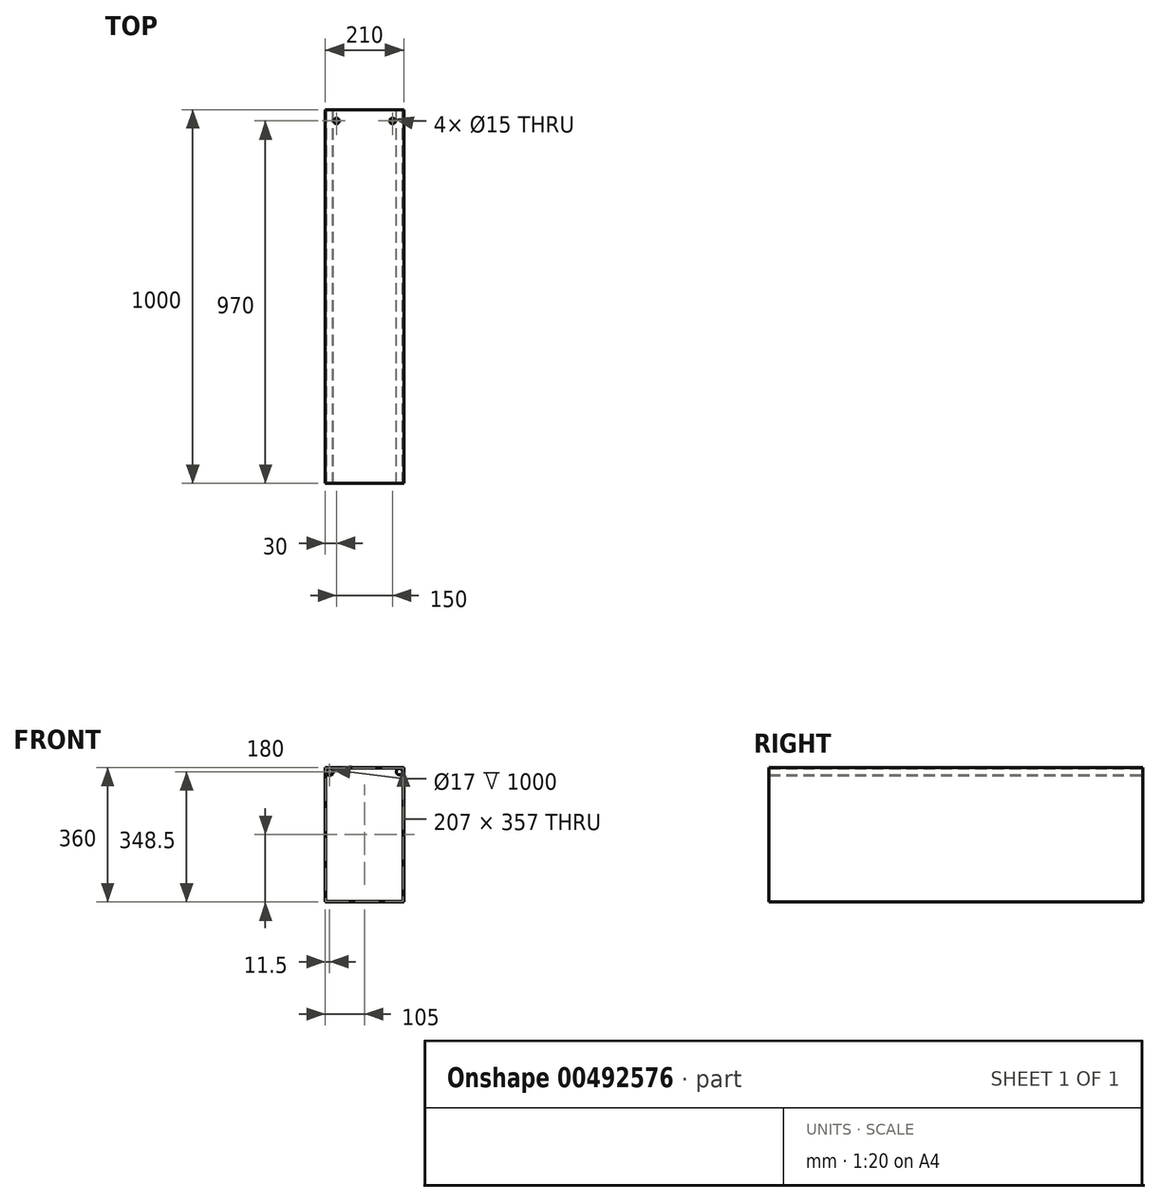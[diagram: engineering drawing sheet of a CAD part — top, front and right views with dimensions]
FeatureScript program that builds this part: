
annotation { "Feature Type Name" : "Feature", "Feature Type Description" : "" }
export const myFeature = defineFeature(function(context is Context, id is Id, definition is map)
    precondition{}
    {
        {
            var Q0;
            Q0=qCreatedBy(makeId("Front.planeOp"),FACE);
            var sketch = newSketch(context, id + "F0", { "sketchPlane" : qUnion([Q0])});
            skLineSegment(sketch, "E0.bottom", {"start": v(0, 0) * mm, "end": v(210, 0) * mm});
            skLineSegment(sketch, "E0.top", {"start": v(0, 360) * mm, "end": v(210, 360) * mm});
            skLineSegment(sketch, "E0.left", {"start": v(0, 0) * mm, "end": v(0, 360) * mm});
            skLineSegment(sketch, "E0.right", {"start": v(210, 0) * mm, "end": v(210, 360) * mm});
            skLineSegment(sketch, "E1.0", {"start": v(1.5, 358.5) * mm, "end": v(208.5, 358.5) * mm});
            skLineSegment(sketch, "E1.1", {"start": v(1.5, 1.5) * mm, "end": v(1.5, 358.5) * mm});
            skLineSegment(sketch, "E1.2", {"start": v(1.5, 1.5) * mm, "end": v(208.5, 1.5) * mm});
            skLineSegment(sketch, "E1.3", {"start": v(208.5, 1.5) * mm, "end": v(208.5, 358.5) * mm});
            skCircle(sketch, "E2", {"center": v(11.5, 348.5) * mm, "radius": 10 * mm});
            skCircle(sketch, "E3.0", {"center": v(11.5, 348.5) * mm, "radius": 8.5 * mm});
            skLineSegment(sketch, "E4", {"start": v(105, 358.5) * mm, "end": v(105, 303.52) * mm, "construction": true});
            skCircle(sketch, "E5.MirrorC", {"center": v(198.5, 348.5) * mm, "radius": 8.5 * mm});
            skCircle(sketch, "E6.MirrorC", {"center": v(198.5, 348.5) * mm, "radius": 10 * mm});
            skSolve(sketch);
        }
        {
            var Q0;
            Q0=makeQuery(id+"F0.imprint","IMPRINT",FACE,{"disambiguationData":[TD([[makeQuery(id+"F0.imprint","IMPRINT",EDGE,{"derivedFrom":sQuery(id+"F0.wireOp",EDGE,"E0.bottom")}),1.0]])]});
            var Q1;
            Q1=makeQuery(id+"F0.imprint","IMPRINT",FACE,{"disambiguationData":[TD([[makeQuery(id+"F0.imprint","IMPRINT",EDGE,{"derivedFrom":sQuery(id+"F0.wireOp",EDGE,"E5.MirrorC")}),1.0]])]});
            var Q2;
            Q2=makeQuery(id+"F0.imprint","IMPRINT",FACE,{"disambiguationData":[TD([[makeQuery(id+"F0.imprint","IMPRINT",EDGE,{"derivedFrom":sQuery(id+"F0.wireOp",EDGE,"E3.0")}),-1.0]])]});
            extrude(context, id + "F1", {"entities" : qUnion([Q0, Q1, Q2]), "depth" : 1000 * mm, "offsetDistance" : 25 * mm});
        }
        {
            var Q0;
            Q0=makeQuery(id+"F1.opExtrude","SWEPT_FACE",FACE,{"disambiguationData":[OSD([sQuery(id+"F0.wireOp",EDGE,"E0.top")])]});
            var sketch = newSketch(context, id + "F2", { "sketchPlane" : qUnion([Q0])});
            skLineSegment(sketch, "E7", {"start": v(105, 0) * mm, "end": v(105, -65.7) * mm, "construction": true});
            skLineSegment(sketch, "E8", {"start": v(26.92, -30) * mm, "end": v(193.26, -30) * mm, "construction": true});
            skPoint(sketch, "E9", {"position": v(30, -30) * mm});
            skPoint(sketch, "E10", {"position": v(180, -30) * mm});
            skSolve(sketch);
        }
        {
            var Q0;
            Q0=sQuery(id+"F2.wireOp",VERTEX,"E10");
            var Q1;
            Q1=sQuery(id+"F2.wireOp",VERTEX,"E9");
            var Q2;
            Q2=makeQuery(id+"F1.opExtrude","SWEPT_BODY",BODY,{"disambiguationData":[OSD([sQuery(id+"F0.wireOp",EDGE,"E0.bottom"),sQuery(id+"F0.wireOp",EDGE,"E0.top"),sQuery(id+"F0.wireOp",EDGE,"E0.left"),sQuery(id+"F0.wireOp",EDGE,"E0.right"),sQuery(id+"F0.wireOp",EDGE,"E1.0"),sQuery(id+"F0.wireOp",EDGE,"E1.1"),sQuery(id+"F0.wireOp",EDGE,"E1.2"),sQuery(id+"F0.wireOp",EDGE,"E1.3")])]});
            hole(context, id + "F3", {"style" : HoleStyle.SIMPLE, "endStyle" : HoleEndStyle.THROUGH, "standardTappedOrClearance" : lookupTablePath({ "standard" : "ISO", "size" : "15", "type" : "Drilled" }), "standardBlindInLast" : lookupTablePath({ "standard" : "ISO", "size" : "15", "type" : "Drilled" }), "holeDiameter" : 15 * mm, "majorDiameter" : 5 * mm, "isTappedThrough" : true, "tappedDepth" : 12 * mm, "tapClearance" : 3, "startFromSketch" : true, "locations" : qUnion([Q0, Q1]), "scope" : qUnion([Q2])});
        }
    });
